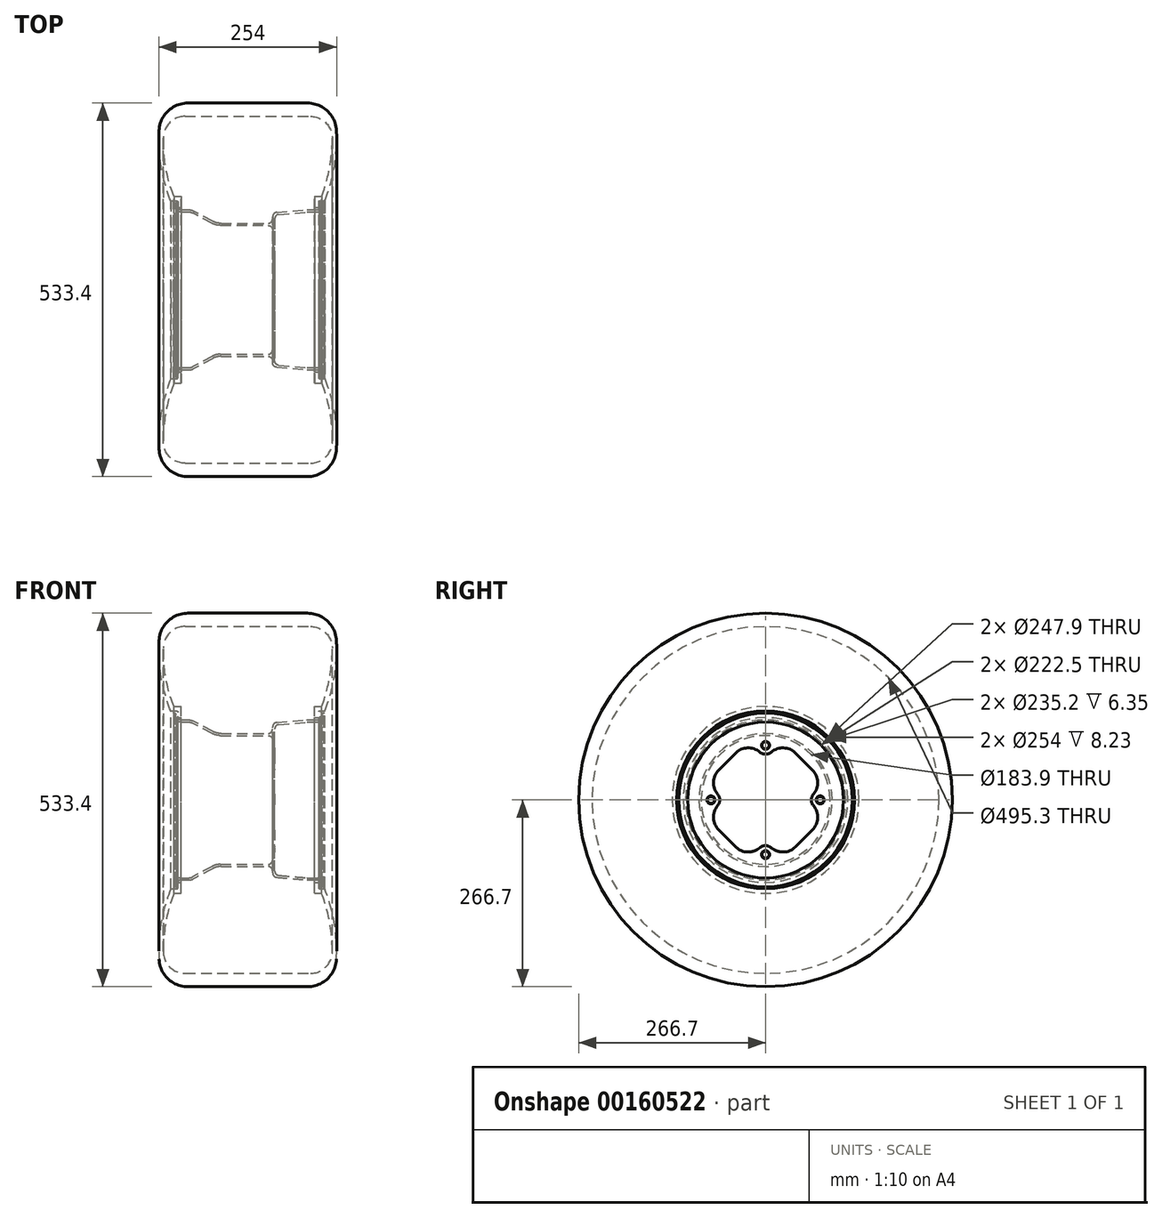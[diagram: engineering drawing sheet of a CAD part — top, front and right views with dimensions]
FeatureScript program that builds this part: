
annotation { "Feature Type Name" : "Feature", "Feature Type Description" : "" }
export const myFeature = defineFeature(function(context is Context, id is Id, definition is map)
    precondition{}
    {
        {
            var Q0;
            Q0=qCreatedBy(makeId("Front.planeOp"),FACE);
            var sketch = newSketch(context, id + "F0", { "sketchPlane" : qUnion([Q0])});
            skLineSegment(sketch, "E0", {"start": v(-1.7, 123.95) * mm, "end": v(0, 123.95) * mm});
            skLineSegment(sketch, "E1", {"start": v(0, 123.95) * mm, "end": v(0, 127) * mm});
            skLineSegment(sketch, "E2", {"start": v(0, 127) * mm, "end": v(-4.75, 127) * mm});
            skLineSegment(sketch, "E3", {"start": v(-6.35, 125.4) * mm, "end": v(-6.35, 117.6) * mm});
            skLineSegment(sketch, "E4", {"start": v(-9.65, 114.3) * mm, "end": v(-23.27, 114.3) * mm});
            skLineSegment(sketch, "E5", {"start": v(-25.45, 114.2) * mm, "end": v(-68.57, 110.49) * mm});
            skLineSegment(sketch, "E6", {"start": v(-74.37, 104.16) * mm, "end": v(-74.37, 101.35) * mm});
            skLineSegment(sketch, "E7", {"start": v(-80.72, 95) * mm, "end": v(-148.03, 95) * mm});
            skLineSegment(sketch, "E8", {"start": v(-159.98, 97.98) * mm, "end": v(-187.77, 112.8) * mm});
            skLineSegment(sketch, "E9", {"start": v(-193.75, 114.3) * mm, "end": v(-206.27, 114.3) * mm});
            skLineSegment(sketch, "E10", {"start": v(-209.58, 117.6) * mm, "end": v(-209.58, 125.4) * mm});
            skLineSegment(sketch, "E11", {"start": v(-211.18, 127) * mm, "end": v(-215.93, 127) * mm});
            skLineSegment(sketch, "E12", {"start": v(-215.93, 127) * mm, "end": v(-215.93, 123.95) * mm});
            skLineSegment(sketch, "E13", {"start": v(-215.93, 123.95) * mm, "end": v(-214.22, 123.95) * mm});
            skLineSegment(sketch, "E14", {"start": v(-212.62, 122.35) * mm, "end": v(-212.62, 117.6) * mm});
            skLineSegment(sketch, "E15", {"start": v(-206.27, 111.25) * mm, "end": v(-194.51, 111.25) * mm});
            skLineSegment(sketch, "E16", {"start": v(-188.54, 109.76) * mm, "end": v(-160.75, 94.94) * mm});
            skLineSegment(sketch, "E17", {"start": v(-148.8, 91.95) * mm, "end": v(-80.72, 91.95) * mm});
            skLineSegment(sketch, "E18", {"start": v(-74.37, 85.6) * mm, "end": v(-74.37, 0) * mm});
            skLineSegment(sketch, "E19", {"start": v(-74.37, 0) * mm, "end": v(-71.32, 0) * mm});
            skLineSegment(sketch, "E20", {"start": v(-71.32, 0) * mm, "end": v(-71.32, 101.37) * mm});
            skLineSegment(sketch, "E21", {"start": v(-65.52, 107.7) * mm, "end": v(-25.45, 111.16) * mm});
            skLineSegment(sketch, "E22", {"start": v(-23.27, 111.25) * mm, "end": v(-9.65, 111.25) * mm});
            skLineSegment(sketch, "E23", {"start": v(-3.3, 117.6) * mm, "end": v(-3.3, 122.35) * mm});
            skLineSegment(sketch, "E24", {"start": v(-3.74, 0) * mm, "end": v(-215.93, 0) * mm, "construction": true});
            skPoint(sketch, "E25.visualSharp", {"position": v(-74.37, 91.95) * mm});
            skArc(sketch, "E25.filletArc", {"start": v(-74.37, 85.6) * mm, "mid": v(-76.23, 90.09) * mm, "end": v(-80.72, 91.95) * mm});
            skPoint(sketch, "E26.visualSharp", {"position": v(-74.37, 95) * mm});
            skArc(sketch, "E26.filletArc", {"start": v(-80.72, 95) * mm, "mid": v(-76.23, 96.86) * mm, "end": v(-74.37, 101.35) * mm});
            skPoint(sketch, "E27.visualSharp", {"position": v(-74.37, 109.99) * mm});
            skArc(sketch, "E27.filletArc", {"start": v(-68.57, 110.49) * mm, "mid": v(-72.7, 108.45) * mm, "end": v(-74.37, 104.16) * mm});
            skPoint(sketch, "E28.visualSharp", {"position": v(-71.32, 107.2) * mm});
            skArc(sketch, "E28.filletArc", {"start": v(-65.52, 107.7) * mm, "mid": v(-69.65, 105.67) * mm, "end": v(-71.32, 101.37) * mm});
            skPoint(sketch, "E29.visualSharp", {"position": v(-6.35, 114.3) * mm});
            skArc(sketch, "E29.filletArc", {"start": v(-9.65, 114.3) * mm, "mid": v(-7.32, 115.27) * mm, "end": v(-6.35, 117.6) * mm});
            skPoint(sketch, "E30.visualSharp", {"position": v(-3.3, 111.25) * mm});
            skArc(sketch, "E30.filletArc", {"start": v(-9.65, 111.25) * mm, "mid": v(-5.16, 113.11) * mm, "end": v(-3.3, 117.6) * mm});
            skPoint(sketch, "E31.visualSharp", {"position": v(-212.62, 111.25) * mm});
            skArc(sketch, "E31.filletArc", {"start": v(-212.62, 117.6) * mm, "mid": v(-210.76, 113.11) * mm, "end": v(-206.27, 111.25) * mm});
            skPoint(sketch, "E32.visualSharp", {"position": v(-209.58, 114.3) * mm});
            skArc(sketch, "E32.filletArc", {"start": v(-209.58, 117.6) * mm, "mid": v(-208.6, 115.27) * mm, "end": v(-206.27, 114.3) * mm});
            skPoint(sketch, "E33.visualSharp", {"position": v(-3.3, 123.95) * mm});
            skArc(sketch, "E33.filletArc", {"start": v(-1.7, 123.95) * mm, "mid": v(-2.83, 123.48) * mm, "end": v(-3.3, 122.35) * mm});
            skPoint(sketch, "E34.visualSharp", {"position": v(-6.35, 127) * mm});
            skArc(sketch, "E34.filletArc", {"start": v(-4.75, 127) * mm, "mid": v(-5.88, 126.53) * mm, "end": v(-6.35, 125.4) * mm});
            skPoint(sketch, "E35.visualSharp", {"position": v(-212.62, 123.95) * mm});
            skArc(sketch, "E35.filletArc", {"start": v(-212.62, 122.35) * mm, "mid": v(-213.1, 123.48) * mm, "end": v(-214.22, 123.95) * mm});
            skPoint(sketch, "E36.visualSharp", {"position": v(-209.58, 127) * mm});
            skArc(sketch, "E36.filletArc", {"start": v(-209.58, 125.4) * mm, "mid": v(-210.04, 126.53) * mm, "end": v(-211.18, 127) * mm});
            skPoint(sketch, "E37.visualSharp", {"position": v(-154.38, 95) * mm});
            skArc(sketch, "E37.filletArc", {"start": v(-159.98, 97.98) * mm, "mid": v(-154.2, 95.75) * mm, "end": v(-148.03, 95) * mm});
            skPoint(sketch, "E38.visualSharp", {"position": v(-155.14, 91.95) * mm});
            skArc(sketch, "E38.filletArc", {"start": v(-160.75, 94.94) * mm, "mid": v(-154.95, 92.7) * mm, "end": v(-148.8, 91.95) * mm});
            skPoint(sketch, "E39.visualSharp", {"position": v(-24.36, 114.3) * mm});
            skArc(sketch, "E39.filletArc", {"start": v(-23.27, 114.3) * mm, "mid": v(-24.36, 114.28) * mm, "end": v(-25.45, 114.2) * mm});
            skPoint(sketch, "E40.visualSharp", {"position": v(-24.36, 111.25) * mm});
            skArc(sketch, "E40.filletArc", {"start": v(-23.27, 111.25) * mm, "mid": v(-24.36, 111.23) * mm, "end": v(-25.45, 111.16) * mm});
            skPoint(sketch, "E41.visualSharp", {"position": v(-190.58, 114.3) * mm});
            skArc(sketch, "E41.filletArc", {"start": v(-187.77, 112.8) * mm, "mid": v(-190.67, 113.92) * mm, "end": v(-193.75, 114.3) * mm});
            skPoint(sketch, "E42.visualSharp", {"position": v(-191.34, 111.25) * mm});
            skArc(sketch, "E42.filletArc", {"start": v(-188.54, 109.76) * mm, "mid": v(-191.43, 110.87) * mm, "end": v(-194.51, 111.25) * mm});
            skSolve(sketch);
        }
        {
            var Q0;
            Q0=qCreatedBy(makeId("Front.planeOp"),FACE);
            var sketch = newSketch(context, id + "F1", { "sketchPlane" : qUnion([Q0])});
            skLineSegment(sketch, "E43", {"start": v(-8.23, 117.6) * mm, "end": v(-8.23, 127) * mm});
            skLineSegment(sketch, "E44.0", {"start": v(-3.74, 0) * mm, "end": v(-215.93, 0) * mm, "construction": true});
            skPoint(sketch, "E45", {"position": v(-109.83, 0) * mm});
            skLineSegment(sketch, "E46", {"start": v(-109.83, 0) * mm, "end": v(-109.83, 259.09) * mm, "construction": true});
            skLineSegment(sketch, "E47", {"start": v(-109.83, 266.7) * mm, "end": v(-24.44, 266.7) * mm});
            skLineSegment(sketch, "E48", {"start": v(-8.23, 127) * mm, "end": v(0, 127) * mm});
            skArc(sketch, "E49", {"start": v(0, 127) * mm, "mid": v(13.88, 176.27) * mm, "end": v(16.88, 227.37) * mm});
            skArc(sketch, "E50", {"start": v(16.88, 227.37) * mm, "mid": v(4.08, 255.3) * mm, "end": v(-24.44, 266.7) * mm});
            skLineSegment(sketch, "E51", {"start": v(-109.83, 247.65) * mm, "end": v(-20.38, 247.65) * mm});
            skArc(sketch, "E52", {"start": v(-20.38, 247.65) * mm, "mid": v(1.64, 238.56) * mm, "end": v(10.82, 216.58) * mm});
            skArc(sketch, "E53.0", {"start": v(-4.33, 133.35) * mm, "mid": v(7.08, 174.27) * mm, "end": v(10.82, 216.58) * mm});
            skLineSegment(sketch, "E53.1", {"start": v(-14.58, 133.35) * mm, "end": v(-4.33, 133.35) * mm});
            skLineSegment(sketch, "E53.2", {"start": v(-14.58, 117.6) * mm, "end": v(-14.58, 133.35) * mm});
            skLineSegment(sketch, "E54", {"start": v(-14.58, 117.6) * mm, "end": v(-8.23, 117.6) * mm});
            skLineSegment(sketch, "E55.MirrorCS", {"start": v(-211.43, 117.6) * mm, "end": v(-211.43, 127) * mm});
            skLineSegment(sketch, "E56.MirrorCS", {"start": v(-205.08, 117.6) * mm, "end": v(-211.43, 117.6) * mm});
            skLineSegment(sketch, "E57.MirrorCS", {"start": v(-211.43, 127) * mm, "end": v(-219.66, 127) * mm});
            skLineSegment(sketch, "E58.MirrorCS", {"start": v(-205.08, 133.35) * mm, "end": v(-215.33, 133.35) * mm});
            skLineSegment(sketch, "E59.MirrorCS", {"start": v(-205.08, 117.6) * mm, "end": v(-205.08, 133.35) * mm});
            skArc(sketch, "E60.MirrorCS", {"start": v(-215.33, 133.35) * mm, "mid": v(-226.74, 174.27) * mm, "end": v(-230.48, 216.58) * mm});
            skArc(sketch, "E61.MirrorCS", {"start": v(-199.28, 247.65) * mm, "mid": v(-221.3, 238.56) * mm, "end": v(-230.48, 216.58) * mm});
            skLineSegment(sketch, "E62.MirrorCS", {"start": v(-109.83, 247.65) * mm, "end": v(-199.28, 247.65) * mm});
            skLineSegment(sketch, "E63.MirrorCS", {"start": v(-109.83, 266.7) * mm, "end": v(-195.22, 266.7) * mm});
            skArc(sketch, "E64.MirrorCS", {"start": v(-236.54, 227.37) * mm, "mid": v(-223.74, 255.3) * mm, "end": v(-195.22, 266.7) * mm});
            skArc(sketch, "E65.MirrorCS", {"start": v(-219.66, 127) * mm, "mid": v(-233.54, 176.27) * mm, "end": v(-236.54, 227.37) * mm});
            skSolve(sketch);
        }
        {
            var Q0;
            Q0=makeQuery(id+"F0.imprint","IMPRINT",FACE,{"disambiguationData":[TD([[makeQuery(id+"F0.imprint","IMPRINT",EDGE,{"derivedFrom":sQuery(id+"F0.wireOp",EDGE,"E0")}),1.0]])]});
            var Q1;
            Q1=sQuery(id+"F0.wireOp",EDGE,"E24");
            revolve(context, id + "F2", {"entities" : qUnion([Q0]), "axis" : qUnion([Q1]), "revolveType" : RevolveType.FULL});
        }
        {
            var Q0;
            Q0=makeQuery(id+"F2.opRevolve","SWEPT_FACE",FACE,{"disambiguationData":[OSD([sQuery(id+"F0.wireOp",EDGE,"E20")])]});
            var sketch = newSketch(context, id + "F3", { "sketchPlane" : qUnion([Q0])});
            skCircle(sketch, "E66", {"center": v(0, 78) * mm, "radius": 5 * mm});
            skArc(sketch, "E67", {"start": v(0, 65.3) * mm, "mid": v(4.39, 66.08) * mm, "end": v(8.24, 68.33) * mm});
            skLineSegment(sketch, "E68", {"start": v(0, 0) * mm, "end": v(78, 0) * mm, "construction": true});
            skLineSegment(sketch, "E69", {"start": v(0, 78) * mm, "end": v(0, 0) * mm, "construction": true});
            skArc(sketch, "E70", {"start": v(8.24, 68.33) * mm, "mid": v(25.72, 74.38) * mm, "end": v(42.68, 66.96) * mm});
            skLineSegment(sketch, "E71", {"start": v(42.68, 66.96) * mm, "end": v(66.96, 42.68) * mm});
            skArc(sketch, "E72", {"start": v(66.96, 42.68) * mm, "mid": v(74.38, 25.72) * mm, "end": v(68.33, 8.24) * mm});
            skArc(sketch, "E73", {"start": v(68.33, 8.24) * mm, "mid": v(66.08, 4.39) * mm, "end": v(65.3, 0) * mm});
            skLineSegment(sketch, "E74.1.0", {"start": v(-66.96, 42.68) * mm, "end": v(-42.68, 66.96) * mm});
            skArc(sketch, "E74.1.1", {"start": v(-42.68, 66.96) * mm, "mid": v(-25.72, 74.38) * mm, "end": v(-8.24, 68.33) * mm});
            skArc(sketch, "E74.1.2", {"start": v(-68.33, 8.24) * mm, "mid": v(-74.38, 25.72) * mm, "end": v(-66.96, 42.68) * mm});
            skArc(sketch, "E74.1.3", {"start": v(-65.3, 0) * mm, "mid": v(-66.08, 4.39) * mm, "end": v(-68.33, 8.24) * mm});
            skCircle(sketch, "E74.1.4", {"center": v(-78, 0) * mm, "radius": 5 * mm});
            skArc(sketch, "E74.1.5", {"start": v(-8.24, 68.33) * mm, "mid": v(-4.39, 66.08) * mm, "end": v(0, 65.3) * mm});
            skLineSegment(sketch, "E74.2.0", {"start": v(-42.68, -66.96) * mm, "end": v(-66.96, -42.68) * mm});
            skArc(sketch, "E74.2.1", {"start": v(-66.96, -42.68) * mm, "mid": v(-74.38, -25.72) * mm, "end": v(-68.33, -8.24) * mm});
            skArc(sketch, "E74.2.2", {"start": v(-8.24, -68.33) * mm, "mid": v(-25.72, -74.38) * mm, "end": v(-42.68, -66.96) * mm});
            skArc(sketch, "E74.2.3", {"start": v(0, -65.3) * mm, "mid": v(-4.39, -66.08) * mm, "end": v(-8.24, -68.33) * mm});
            skCircle(sketch, "E74.2.4", {"center": v(0, -78) * mm, "radius": 5 * mm});
            skArc(sketch, "E74.2.5", {"start": v(-68.33, -8.24) * mm, "mid": v(-66.08, -4.39) * mm, "end": v(-65.3, 0) * mm});
            skLineSegment(sketch, "E74.3.0", {"start": v(66.96, -42.68) * mm, "end": v(42.68, -66.96) * mm});
            skArc(sketch, "E74.3.1", {"start": v(42.68, -66.96) * mm, "mid": v(25.72, -74.38) * mm, "end": v(8.24, -68.33) * mm});
            skArc(sketch, "E74.3.2", {"start": v(68.33, -8.24) * mm, "mid": v(74.38, -25.72) * mm, "end": v(66.96, -42.68) * mm});
            skArc(sketch, "E74.3.3", {"start": v(65.3, 0) * mm, "mid": v(66.08, -4.39) * mm, "end": v(68.33, -8.24) * mm});
            skCircle(sketch, "E74.3.4", {"center": v(78, 0) * mm, "radius": 5 * mm});
            skArc(sketch, "E74.3.5", {"start": v(8.24, -68.33) * mm, "mid": v(4.39, -66.08) * mm, "end": v(0, -65.3) * mm});
            skPoint(sketch, "E74.center", {"position": v(0, 0) * mm});
            skSolve(sketch);
        }
        {
            var Q0;
            Q0 = qSketchRegion(id + "F3", true);
            extrude(context, id + "F4", {"entities" : qUnion([Q0]), "operationType" : NewBodyOperationType.REMOVE, "endBound" : BoundingType.THROUGH_ALL, "oppositeDirection" : true, "depth" : 25.4 * mm});
        }
        {
            var Q0;
            Q0=makeQuery(id+"F2.opRevolve","SWEPT_FACE",FACE,{"disambiguationData":[OSD([sQuery(id+"F0.wireOp",EDGE,"E1")])]});
            var Q1;
            Q1=makeQuery(id+"F2.opRevolve","SWEPT_FACE",FACE,{"disambiguationData":[OSD([sQuery(id+"F0.wireOp",EDGE,"E12")])]});
            var Q2;
            Q2=makeQuery(id+"F4.boolean.opBoolean","COPY",FACE,{"derivedFrom":makeQuery(id+"F4.opExtrude","SWEPT_FACE",FACE,{"disambiguationData":[OSD([sQuery(id+"F3.wireOp",EDGE,"E74.3.4")])]})});
            var Q3;
            Q3=makeQuery(id+"F4.boolean.opBoolean","COPY",FACE,{"derivedFrom":makeQuery(id+"F4.opExtrude","SWEPT_FACE",FACE,{"disambiguationData":[OSD([sQuery(id+"F3.wireOp",EDGE,"E74.2.4")])]})});
            var Q4;
            Q4=makeQuery(id+"F4.boolean.opBoolean","COPY",EDGE,{"derivedFrom":makeQuery(id+"F4.opExtrude","CAP_EDGE",EDGE,{"disambiguationData":[OSD([sQuery(id+"F3.wireOp",EDGE,"E74.3.0")])],"isStart":true})});
            var Q5;
            Q5=makeQuery(id+"F4.boolean.opBoolean","INTERSECT",EDGE,{"derivedFrom":[makeQuery(id+"F2.opRevolve","SWEPT_FACE",FACE,{"disambiguationData":[OSD([sQuery(id+"F0.wireOp",EDGE,"E18")])]}),makeQuery(id+"F4.opExtrude","SWEPT_FACE",FACE,{"disambiguationData":[OSD([sQuery(id+"F3.wireOp",EDGE,"E74.3.0")])]})]});
            var Q6;
            Q6=makeQuery(id+"F4.boolean.opBoolean","COPY",FACE,{"derivedFrom":makeQuery(id+"F4.opExtrude","SWEPT_FACE",FACE,{"disambiguationData":[OSD([sQuery(id+"F3.wireOp",EDGE,"E74.1.4")])]})});
            var Q7;
            Q7=makeQuery(id+"F4.boolean.opBoolean","COPY",FACE,{"derivedFrom":makeQuery(id+"F4.opExtrude","SWEPT_FACE",FACE,{"disambiguationData":[OSD([sQuery(id+"F3.wireOp",EDGE,"E66")])]})});
            chamfer(context, id + "F5", {"entities" : qUnion([Q0, Q1, Q2, Q3, Q4, Q5, Q6, Q7]), "width" : 0.76 * mm, "tangentPropagation" : true});
        }
        {
            var Q0;
            Q0 = qSketchRegion(id + "F1", true);
            var Q1;
            Q1=sQuery(id+"F0.wireOp",EDGE,"E24");
            revolve(context, id + "F6", {"entities" : qUnion([Q0]), "axis" : qUnion([Q1]), "revolveType" : RevolveType.FULL});
        }
    });
